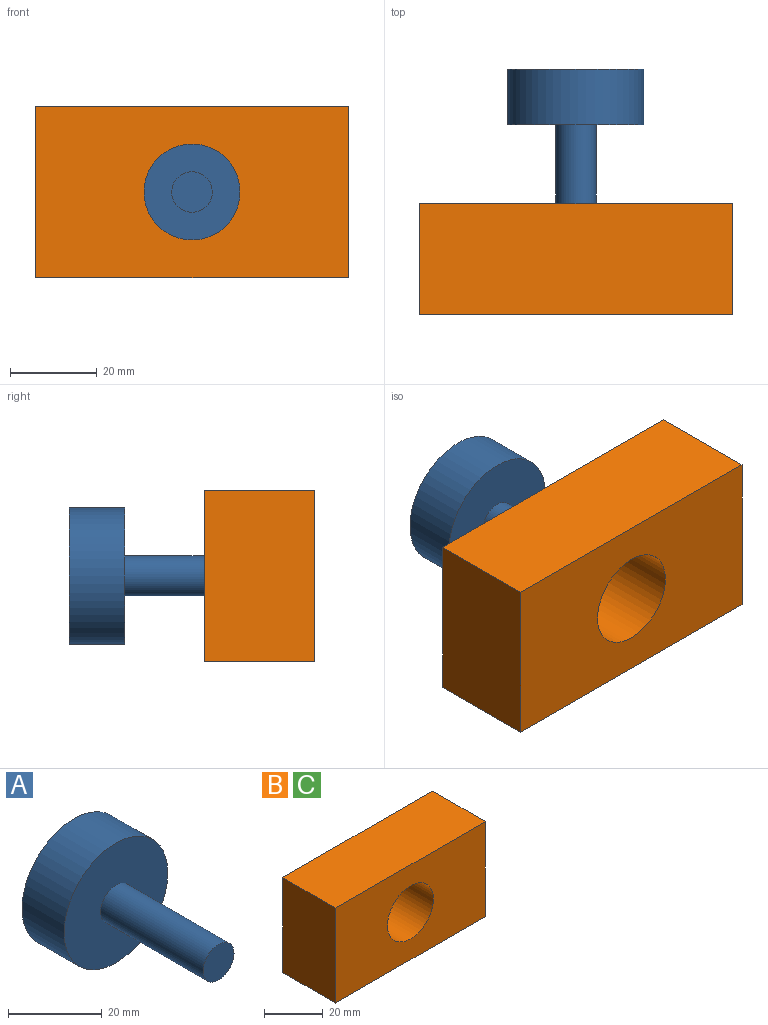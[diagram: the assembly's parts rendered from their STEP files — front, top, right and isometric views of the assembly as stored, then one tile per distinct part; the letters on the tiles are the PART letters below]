
ASSEMBLY  parts=3 mates=1
PART A: 5 faces, bbox 31.3x43.7x31.3 mm
  f0: plane 9.32x9.32mm, normal (0,-1,0), area 68.3mm2, adj f1
  f1: cylinder r=4.66mm len=30.98mm, axis (0,1,0), area 907.6mm2, adj f0,f4
  f2: cylinder r=15.65mm len=31.31mm, axis (0,-1,0), area 1249.1mm2, adj f3,f4
  f3: plane 31.31x31.31mm, normal (0,1,0), area 769.8mm2, adj f2
  f4: plane 31.31x31.31mm, normal (0,-1,0), area 701.6mm2, adj f1,f2
PART B: 7 faces, bbox 71.9x25.4x39.4 mm
  f0: plane 39.4x25.4mm, normal (-1,0,0), area 1000.8mm2, adj f1,f4,f5,f6
  f1: plane 71.89x25.4mm, normal (0,0,-1), area 1826mm2, adj f0,f2,f5,f6
  f2: plane 39.4x25.4mm, normal (1,0,0), area 1000.8mm2, adj f1,f4,f5,f6
  f3: cylinder r=11.04mm len=25.4mm, axis (0,1,0), area 1761.5mm2, adj f5,f6
  f4: plane 71.89x25.4mm, normal (0,0,1), area 1826mm2, adj f0,f2,f5,f6
  f5: plane 71.89x39.4mm, normal (0,-1,0), area 2449.9mm2, adj f0,f1,f2,f3,f4
  f6: plane 71.89x39.4mm, normal (0,1,0), area 2449.9mm2, adj f0,f1,f2,f3,f4
PART C: same geometry as B
PLACE A t=(-113.36,-155.58,-68.11)mm
PLACE B t=(-113.36,-123.18,-68.11)mm
PLACE C t=(-113.36,-123.18,-68.11)mm fixed
MATE slider C.f3 <-> A.f1  axis (0,1,0) through (-113.36,-123.18,-68.11)mm
